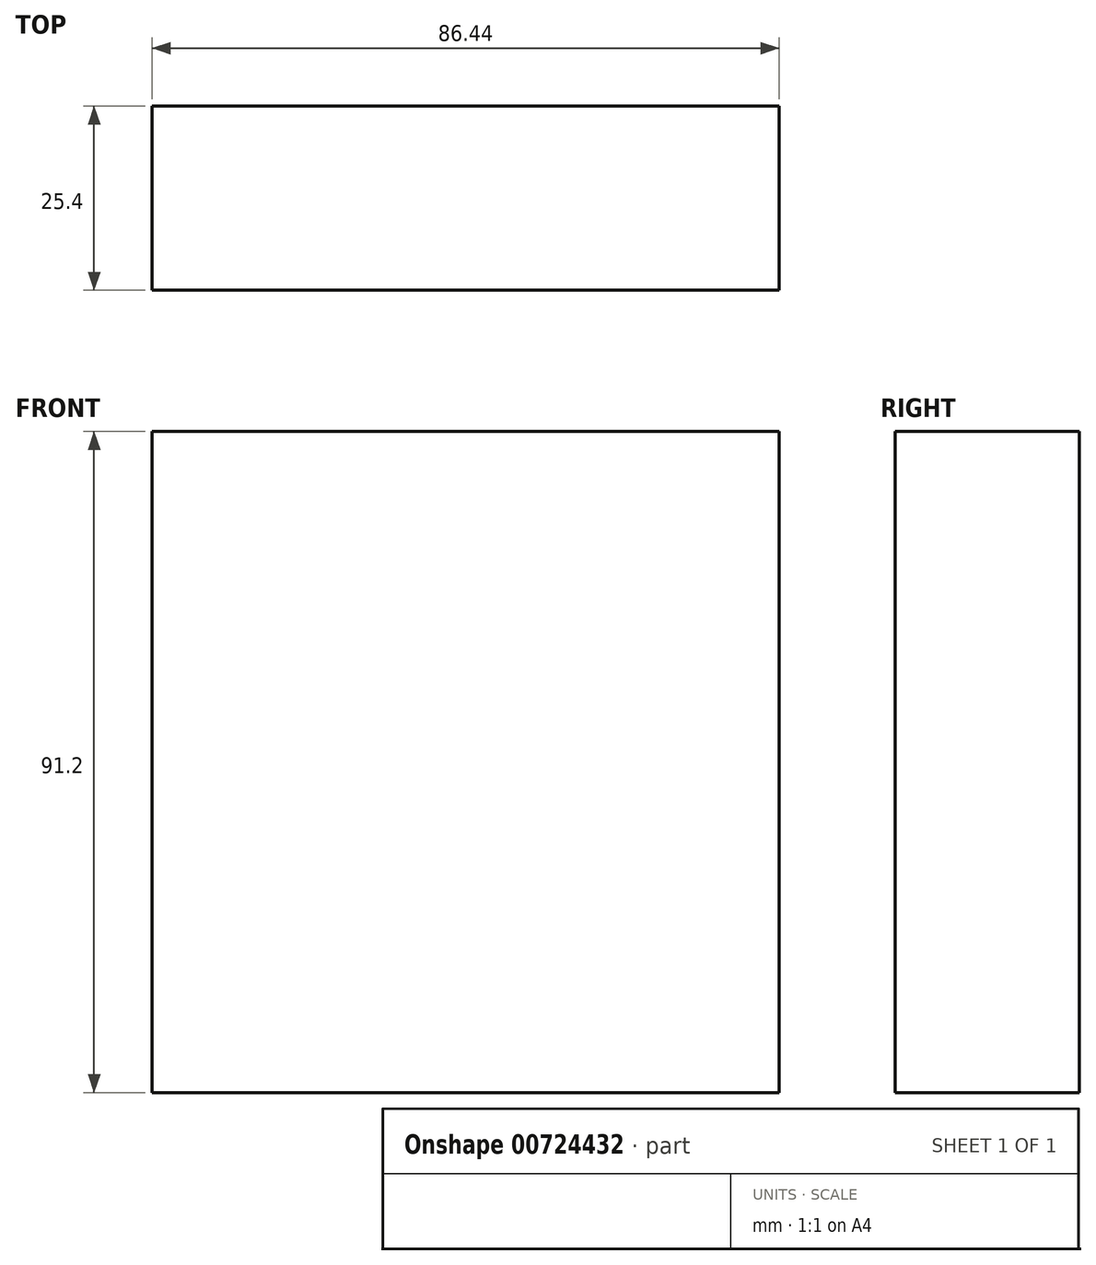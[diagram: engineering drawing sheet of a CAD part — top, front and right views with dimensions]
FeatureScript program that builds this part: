
annotation { "Feature Type Name" : "Feature", "Feature Type Description" : "" }
export const myFeature = defineFeature(function(context is Context, id is Id, definition is map)
    precondition{}
    {
        {
            var Q0;
            Q0=qCreatedBy(makeId("Front.planeOp"),FACE);
            var sketch = newSketch(context, id + "F0", { "sketchPlane" : qUnion([Q0])});
            skLineSegment(sketch, "E0.bottom", {"start": v(43.22, 42.94) * mm, "end": v(-43.22, 42.94) * mm});
            skLineSegment(sketch, "E0.top", {"start": v(43.22, -48.26) * mm, "end": v(-43.22, -48.26) * mm});
            skLineSegment(sketch, "E0.left", {"start": v(43.22, 42.94) * mm, "end": v(43.22, -48.26) * mm});
            skLineSegment(sketch, "E0.right", {"start": v(-43.22, 42.94) * mm, "end": v(-43.22, -48.26) * mm});
            skPoint(sketch, "E0.middle", {"position": v(0, -2.66) * mm});
            skSolve(sketch);
        }
        {
            var Q0;
            Q0=makeQuery(id+"F0.imprint","IMPRINT",FACE,{"disambiguationData":[TD([[makeQuery(id+"F0.imprint","IMPRINT",EDGE,{"derivedFrom":sQuery(id+"F0.wireOp",EDGE,"E0.bottom")}),1.0]])]});
            extrude(context, id + "F1", {"entities" : qUnion([Q0]), "depth" : 25.4 * mm, "offsetDistance" : 25.4 * mm});
        }
    });
